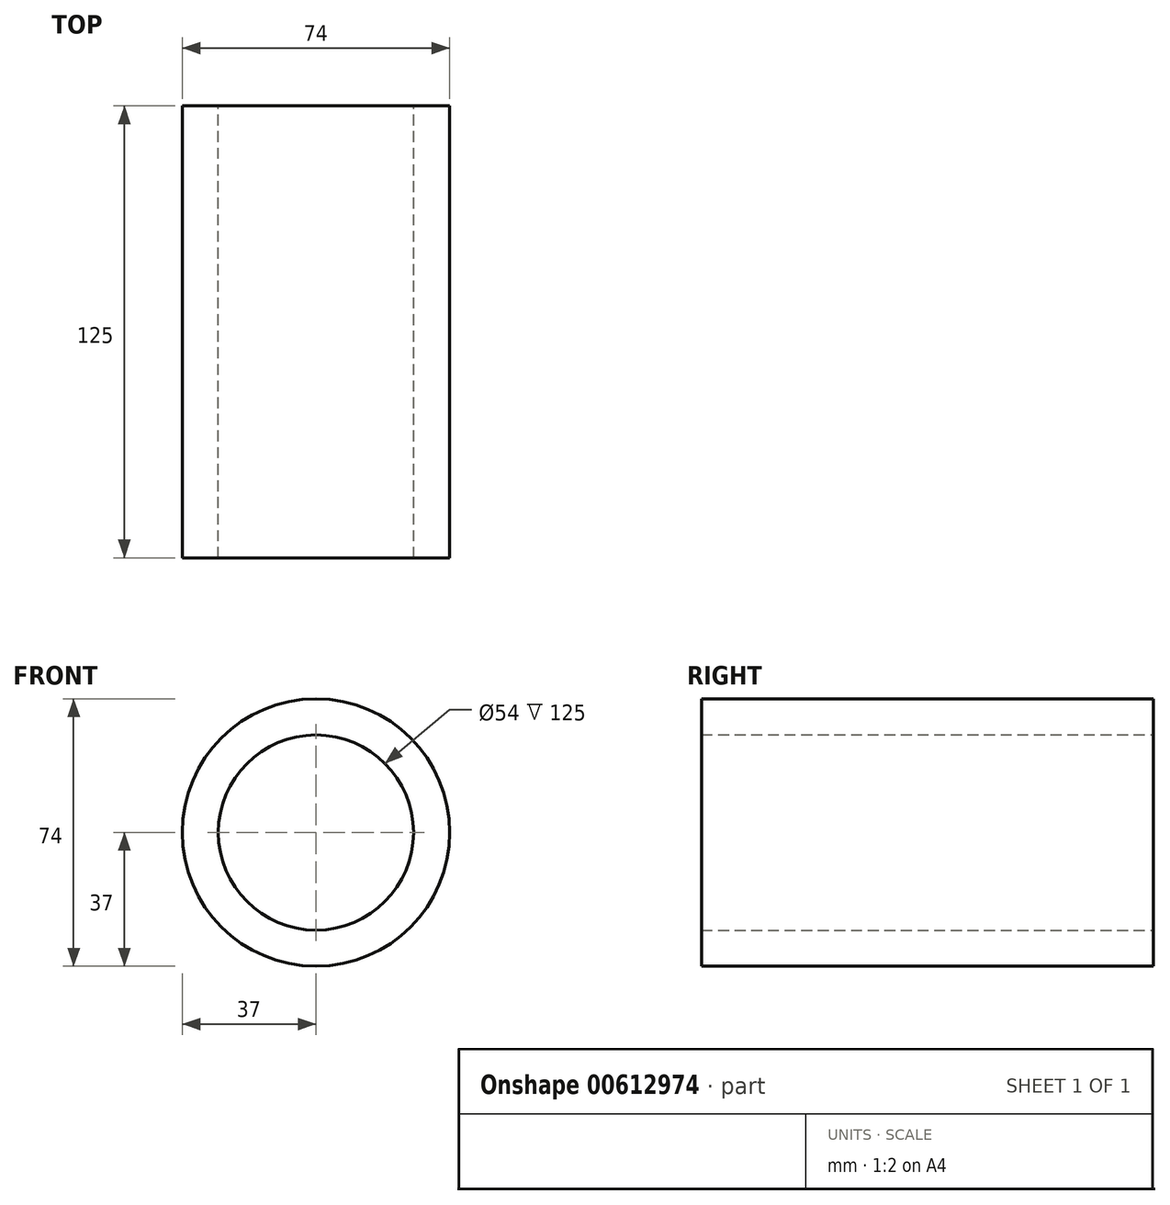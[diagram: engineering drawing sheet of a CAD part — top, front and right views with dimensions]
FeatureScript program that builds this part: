
annotation { "Feature Type Name" : "Feature", "Feature Type Description" : "" }
export const myFeature = defineFeature(function(context is Context, id is Id, definition is map)
    precondition{}
    {
        {
            var Q0;
            Q0=qCreatedBy(makeId("Front.planeOp"),FACE);
            var sketch = newSketch(context, id + "F0", { "sketchPlane" : qUnion([Q0])});
            skCircle(sketch, "E0", {"center": v(0, 0) * mm, "radius": 37 * mm});
            skCircle(sketch, "E1", {"center": v(0, 0) * mm, "radius": 27 * mm});
            skSolve(sketch);
        }
        {
            var Q0;
            Q0=makeQuery(id+"F0.imprint","IMPRINT",FACE,{"disambiguationData":[TD([[makeQuery(id+"F0.imprint","IMPRINT",EDGE,{"derivedFrom":sQuery(id+"F0.wireOp",EDGE,"E0")}),1.0]])]});
            extrude(context, id + "F1", {"entities" : qUnion([Q0]), "depth" : 62.5 * mm, "offsetDistance" : 25 * mm, "hasSecondDirection" : true, "secondDirectionOppositeDirection" : true, "secondDirectionDepth" : 62.5 * mm});
        }
    });
